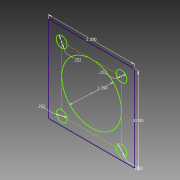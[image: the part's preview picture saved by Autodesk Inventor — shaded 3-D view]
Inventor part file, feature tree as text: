
AUTODESK INVENTOR PART (.ipt)
format: ipt  version: 2013 (Build 170138000, 138)  size: 69,120 bytes
history: native  units: in
note: dims shown in document units (in); Inventor stores cm internally (conversion verified against a paired STEP export)
features: sketch x1
ambient origin geometry x8: Origin, YZ Plane, XZ Plane, XY Plane, X Axis, Y Axis, Z Axis, Center Point
feature tree (1):
  sketch  "Sketch1"  dims[d0=2.0in d1=2.0in d2=1.39in d3=0.252in d4=0.252in d5=0.252in d6=0.252in]
